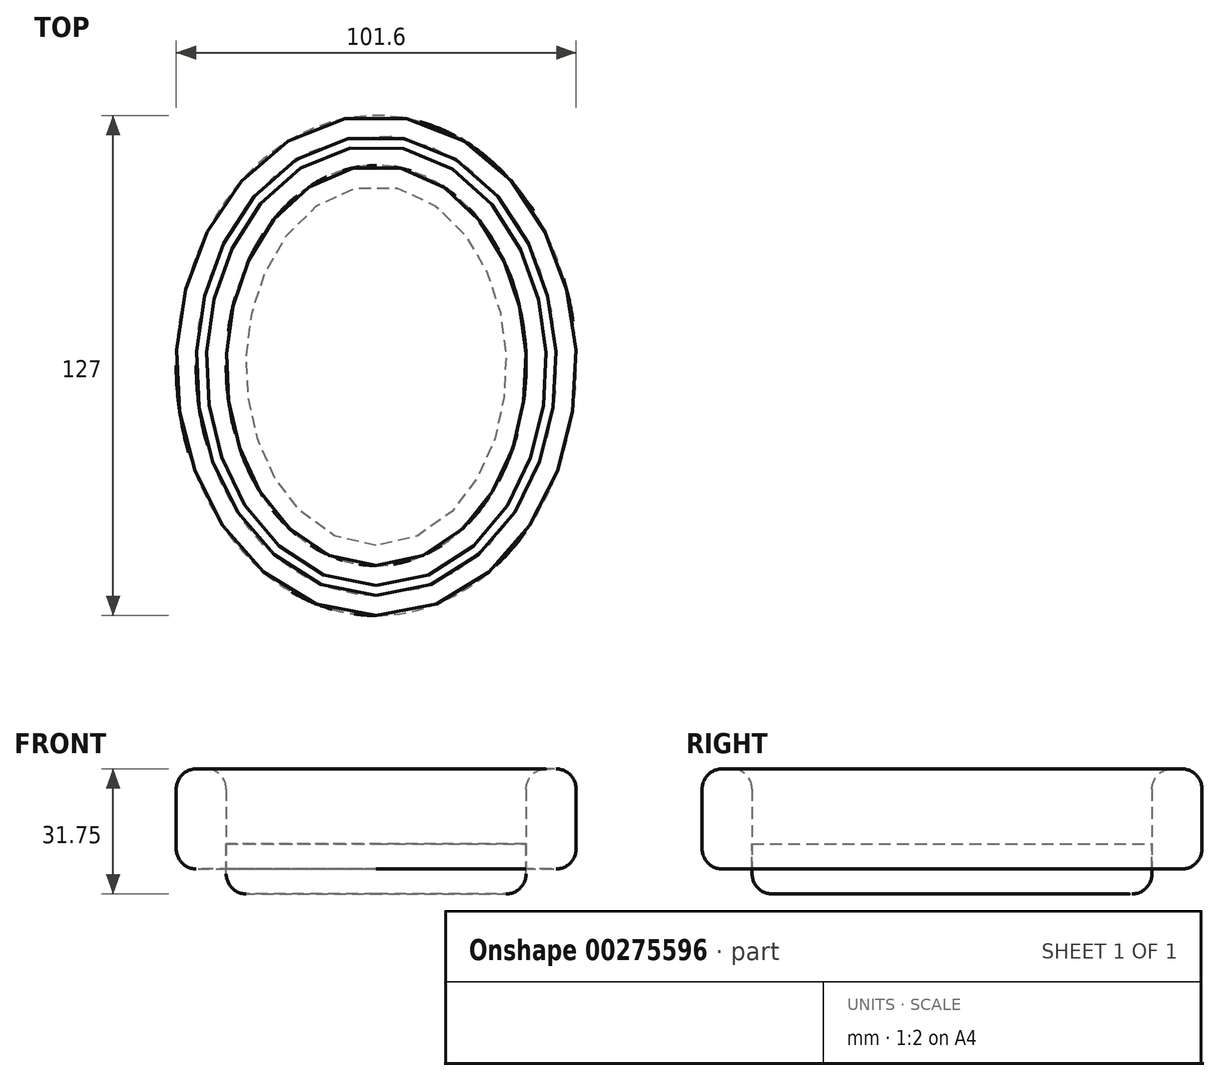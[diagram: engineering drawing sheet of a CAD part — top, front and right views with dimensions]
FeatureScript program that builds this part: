
annotation { "Feature Type Name" : "Feature", "Feature Type Description" : "" }
export const myFeature = defineFeature(function(context is Context, id is Id, definition is map)
    precondition{}
    {
        {
            var Q0;
            Q0=qCreatedBy(makeId("Top.planeOp"),FACE);
            var sketch = newSketch(context, id + "F0", { "sketchPlane" : qUnion([Q0])});
            skEllipse(sketch, "E0", {"center": v(0, 0) * mm, "majorRadius": 63.5 * mm, "minorRadius": 50.8 * mm, "majorAxis": v(0, -1)});
            skEllipse(sketch, "E1", {"center": v(0, 0) * mm, "majorRadius": 50.8 * mm, "minorRadius": 38.1 * mm, "majorAxis": v(0, -1)});
            skSolve(sketch);
        }
        {
            var Q0;
            Q0 = qSketchRegion(id + "F0", true);
            extrude(context, id + "F1", {"entities" : qUnion([Q0]), "depth" : 25.4 * mm});
        }
        {
            var Q0;
            Q0=makeQuery(id+"F0.imprint","IMPRINT",FACE,{"disambiguationData":[TD([[makeQuery(id+"F0.imprint","IMPRINT",EDGE,{"derivedFrom":sQuery(id+"F0.wireOp",EDGE,"E1")}),1.0]])]});
            extrude(context, id + "F2", {"entities" : qUnion([Q0]), "endBound" : BoundingType.SYMMETRIC, "oppositeDirection" : true, "depth" : 12.7 * mm});
        }
        {
            var Q0;
            Q0=makeQuery(id+"F1.opExtrude","CAP_EDGE",EDGE,{"disambiguationData":[OSD([sQuery(id+"F0.wireOp",EDGE,"E0")])],"isStart":false});
            var Q1;
            Q1=makeQuery(id+"F1.opExtrude","CAP_EDGE",EDGE,{"disambiguationData":[OSD([sQuery(id+"F0.wireOp",EDGE,"E1")])],"isStart":false});
            var Q2;
            Q2=makeQuery(id+"F1.opExtrude","CAP_EDGE",EDGE,{"disambiguationData":[OSD([sQuery(id+"F0.wireOp",EDGE,"E0")])],"isStart":true});
            var Q3;
            Q3=makeQuery(id+"F2.opExtrude","CAP_EDGE",EDGE,{"disambiguationData":[OSD([sQuery(id+"F0.wireOp",EDGE,"E1")])],"isStart":false});
            fillet(context, id + "F3", {"entities" : qUnion([Q0, Q1, Q2, Q3]), "radius" : 5.08 * mm, "tangentPropagation" : true, "allowEdgeOverflow" : false});
        }
    });
